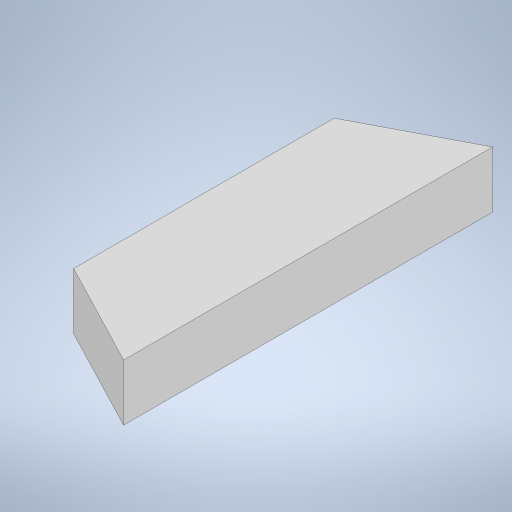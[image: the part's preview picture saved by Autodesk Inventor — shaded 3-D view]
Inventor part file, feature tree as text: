
AUTODESK INVENTOR PART (.ipt)
format: ipt  version: 2023 (Build 270158000, 158)  size: 203,776 bytes
history: native  units: mm
features: extrude x1, sketch x1
ambient origin geometry x8: Origin, YZ Plane, XZ Plane, XY Plane, X Axis, Y Axis, Z Axis, Center Point
bodies: Solid1 (feature_tree)
feature tree (2):
  extrude  "Extrusion1"  Depth=85.0mm
  sketch  "Sketch1"  dims[d1=24.0mm d2=85.0mm d3=60.0mm d4=13.0mm d5=0.0mm]
